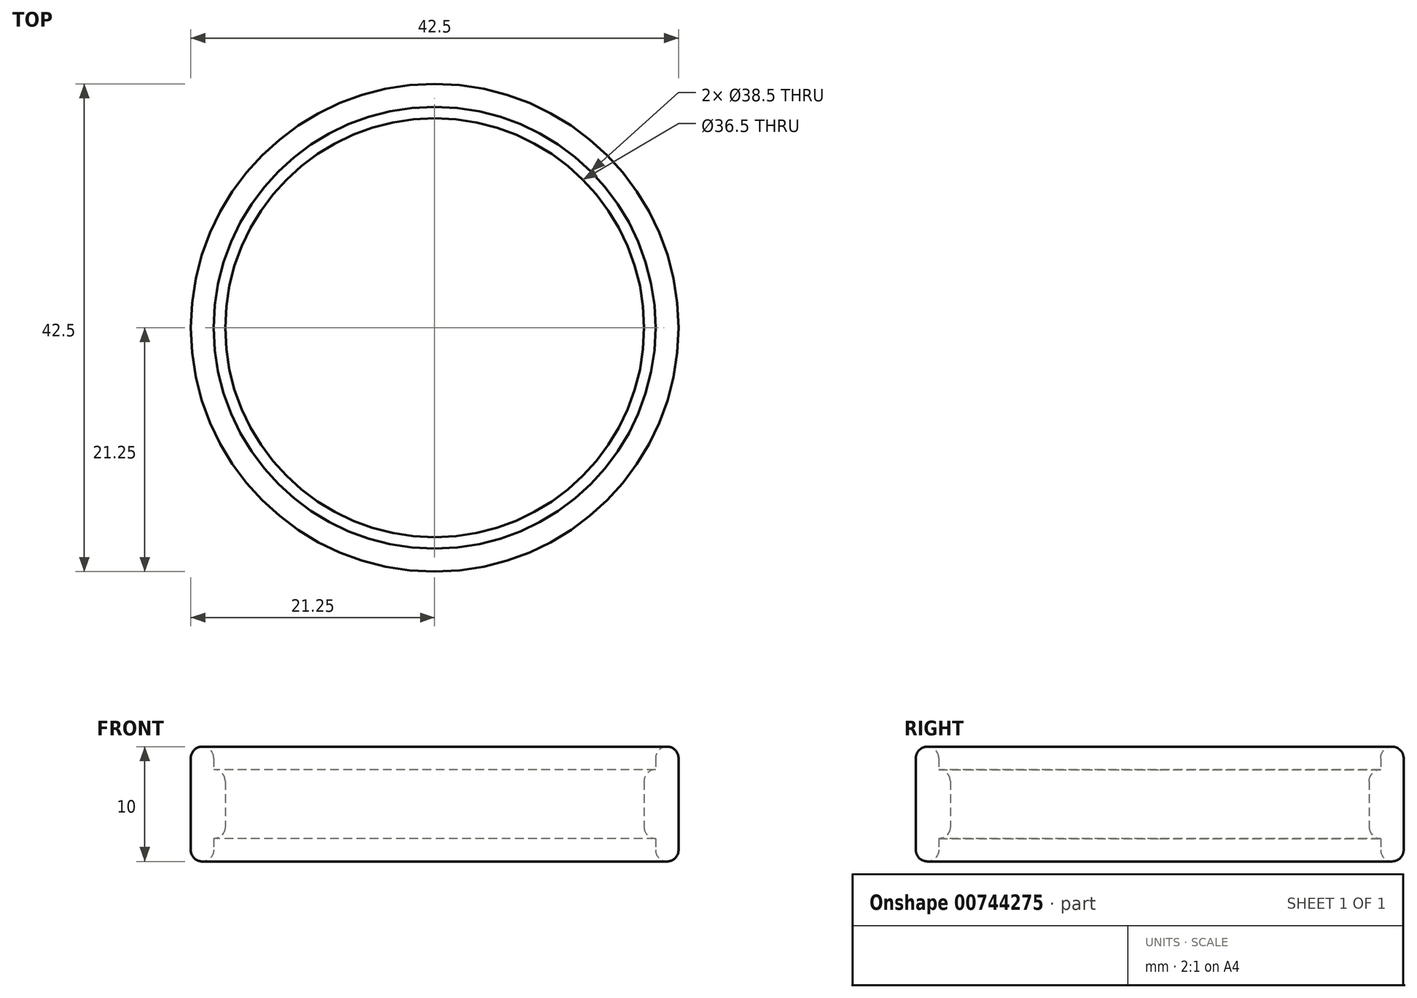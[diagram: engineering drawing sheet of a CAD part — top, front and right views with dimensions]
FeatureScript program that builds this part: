
annotation { "Feature Type Name" : "Feature", "Feature Type Description" : "" }
export const myFeature = defineFeature(function(context is Context, id is Id, definition is map)
    precondition{}
    {
        {
            var Q0;
            Q0=qCreatedBy(makeId("Top.planeOp"),FACE);
            var sketch = newSketch(context, id + "F0", { "sketchPlane" : qUnion([Q0])});
            skCircle(sketch, "E0", {"center": v(0, 0) * mm, "radius": 21.25 * mm});
            skCircle(sketch, "E1", {"center": v(0, 0) * mm, "radius": 19.25 * mm});
            skSolve(sketch);
        }
        {
            var Q0;
            Q0=makeQuery(id+"F0.imprint","IMPRINT",FACE,{"disambiguationData":[TD([[makeQuery(id+"F0.imprint","IMPRINT",EDGE,{"derivedFrom":sQuery(id+"F0.wireOp",EDGE,"E0")}),1.0]])]});
            extrude(context, id + "F1", {"entities" : qUnion([Q0]), "depth" : 10 * mm, "offsetDistance" : 25 * mm});
        }
        {
            var Q0;
            Q0=qCreatedBy(makeId("Top.planeOp"),FACE);
            cPlane(context, id + "F2", {"entities" : qUnion([Q0]), "cplaneType" : CPlaneType.OFFSET, "offset" : 2 * mm, "width" : 150 * mm, "height" : 150 * mm});
        }
        {
            var Q0;
            Q0=qCreatedBy(id+"F2.planeOp",FACE);
            var sketch = newSketch(context, id + "F3", { "sketchPlane" : qUnion([Q0])});
            skCircle(sketch, "E2", {"center": v(0, 0) * mm, "radius": 18.25 * mm});
            skCircle(sketch, "E3", {"center": v(0, 0) * mm, "radius": 21.25 * mm});
            skSolve(sketch);
        }
        {
            var Q0;
            Q0=qSketchRegion(id+"F3",true);
            extrude(context, id + "F4", {"entities" : qUnion([Q0]), "operationType" : NewBodyOperationType.ADD, "depth" : 6 * mm, "offsetDistance" : 25 * mm});
        }
        {
            var Q0;
            Q0=makeQuery(id+"F4.opExtrude","CAP_EDGE",EDGE,{"disambiguationData":[OSD([sQuery(id+"F3.wireOp",EDGE,"E2")])],"isStart":true});
            var Q1;
            Q1=makeQuery(id+"F4.opExtrude","CAP_EDGE",EDGE,{"disambiguationData":[OSD([sQuery(id+"F3.wireOp",EDGE,"E2")])],"isStart":false});
            var Q2;
            Q2=makeQuery(id+"F1.opExtrude","CAP_EDGE",EDGE,{"disambiguationData":[OSD([sQuery(id+"F0.wireOp",EDGE,"E1")])],"isStart":false});
            var Q3;
            Q3=makeQuery(id+"F1.opExtrude","CAP_EDGE",EDGE,{"disambiguationData":[OSD([sQuery(id+"F0.wireOp",EDGE,"E0")])],"isStart":false});
            var Q4;
            Q4=makeQuery(id+"F1.opExtrude","CAP_EDGE",EDGE,{"disambiguationData":[OSD([sQuery(id+"F0.wireOp",EDGE,"E0")])],"isStart":true});
            var Q5;
            Q5=makeQuery(id+"F1.opExtrude","CAP_EDGE",EDGE,{"disambiguationData":[OSD([sQuery(id+"F0.wireOp",EDGE,"E1")])],"isStart":true});
            fillet(context, id + "F5", {"entities" : qUnion([Q0, Q1, Q2, Q3, Q4, Q5]), "radius" : 1 * mm, "tangentPropagation" : true, "allowEdgeOverflow" : false});
        }
    });
